# Revit family: QF_GIORIK_GR1021M_GR1021P
name_source: partatom
category: Specialty Equipment
revit_build: Autodesk Revit 2014 (Build: 20140709_2115(x64)
units: mm (PartAtom-declared; Revit-internal decimal feet)

## types (2) — shared parameters
Apparent Power = 15900 VA
Assembly Code = E1090320
Cold Water Connection Height = 199 mm
Cold Water Size = 1"
Cold Water Temperature Recommended = 0 °C
Cycle = 50 Hz
FL Amps = 0 A
HP = 0
Indirect Waste Connection Height = 46 mm
Indirect Waste Flow = 0.0 L/s
Indirect Waste Size = 1"
Manufacturer = GIORIK
Max Overcurrent Protection = 20 A
Min Ckt Ampacity = 0 A
Phase = 3
URL = www.giorik.com
Volts = 400 V
Waste Water Discharge Temperature = 0 °C
Watts = 15900 W
Weight in Pounds = 337.307

## per-type parameters (varying)
| type | Description | Mechanical control | Programmable electronic control |
| GR1021M | REGENERATING OVEN 10 GN 2/1 - MECHANICAL VERSION | Yes | No |
| GR1021P | HOLDING CABINET-REGENERATOR 10 GN 2/1  - PROGRAMMABLE ELECTRONIC VERSION | No | Yes |

note: column(s) folded — value = type name in every type: Model

## geometry (parser evidence)
native form markers: Sweep x3
no freeform markers — native parametric forms only
